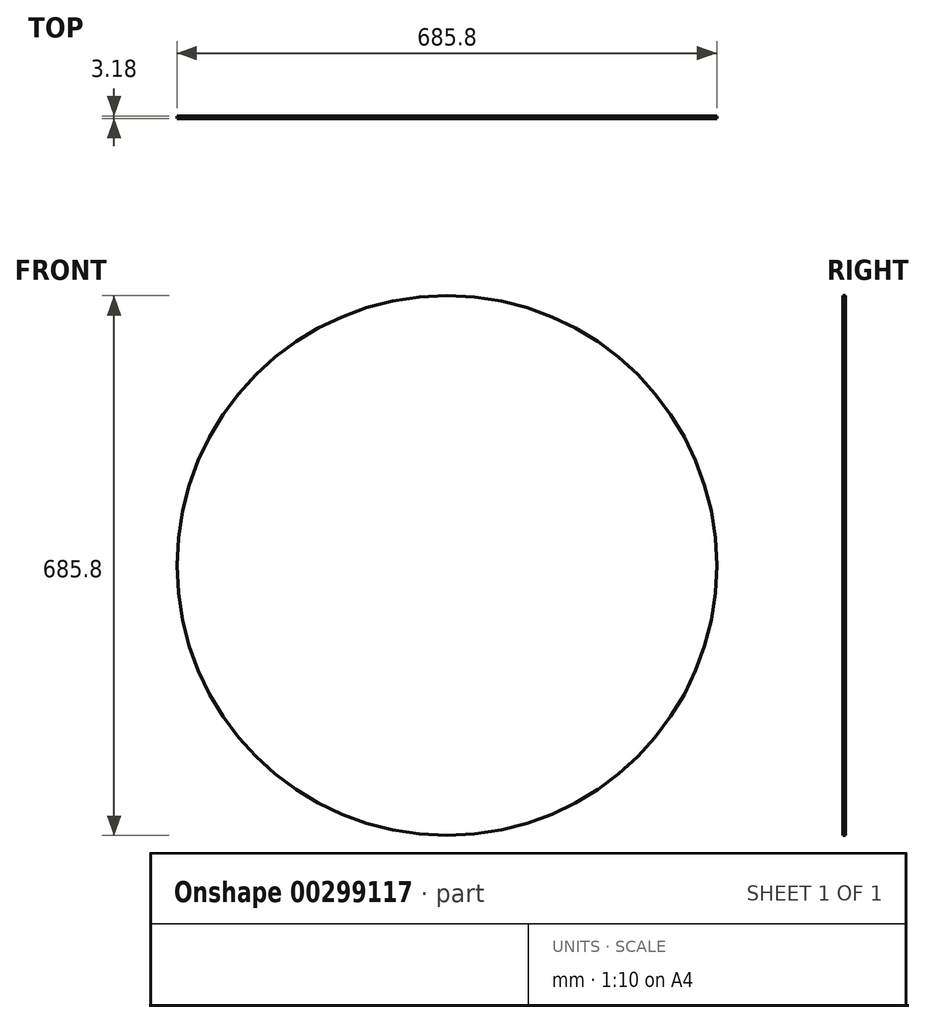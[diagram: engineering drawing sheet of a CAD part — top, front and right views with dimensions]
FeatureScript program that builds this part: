
annotation { "Feature Type Name" : "Feature", "Feature Type Description" : "" }
export const myFeature = defineFeature(function(context is Context, id is Id, definition is map)
    precondition{}
    {
        {
            var Q0;
            Q0=qCreatedBy(makeId("Front.planeOp"),FACE);
            var sketch = newSketch(context, id + "F0", { "sketchPlane" : qUnion([Q0])});
            skCircle(sketch, "E0", {"center": v(0, 0) * mm, "radius": 342.9 * mm});
            skSolve(sketch);
        }
        {
            var Q0;
            Q0 = qSketchRegion(id + "F0", true);
            extrude(context, id + "F1", {"entities" : qUnion([Q0]), "depth" : 3.17 * mm});
        }
    });
